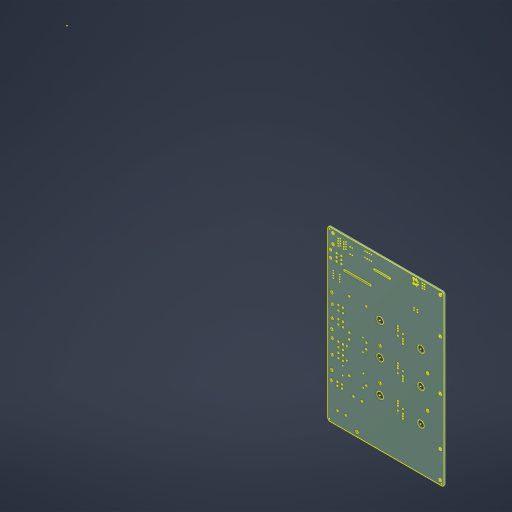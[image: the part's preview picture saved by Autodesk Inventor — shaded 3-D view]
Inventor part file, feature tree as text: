
AUTODESK INVENTOR PART (.ipt)
format: ipt  version: 2024.2 (Build 282272000, 272)  size: 454,144 bytes
history: native  units: in
note: dims shown in document units (in); Inventor stores cm internally (conversion verified against a paired STEP export)
features: sketch x1, projected_geometry x1, imported_body x1
ambient origin geometry x8: Origin, YZ Plane, XZ Plane, XY Plane, X Axis, Y Axis, Z Axis, Center Point
bodies: Solid1 (feature_tree)
feature tree (3):
  sketch  "Sketch1"
  projected_geometry  "Projected Loop1"
  imported_body  "Base1"
